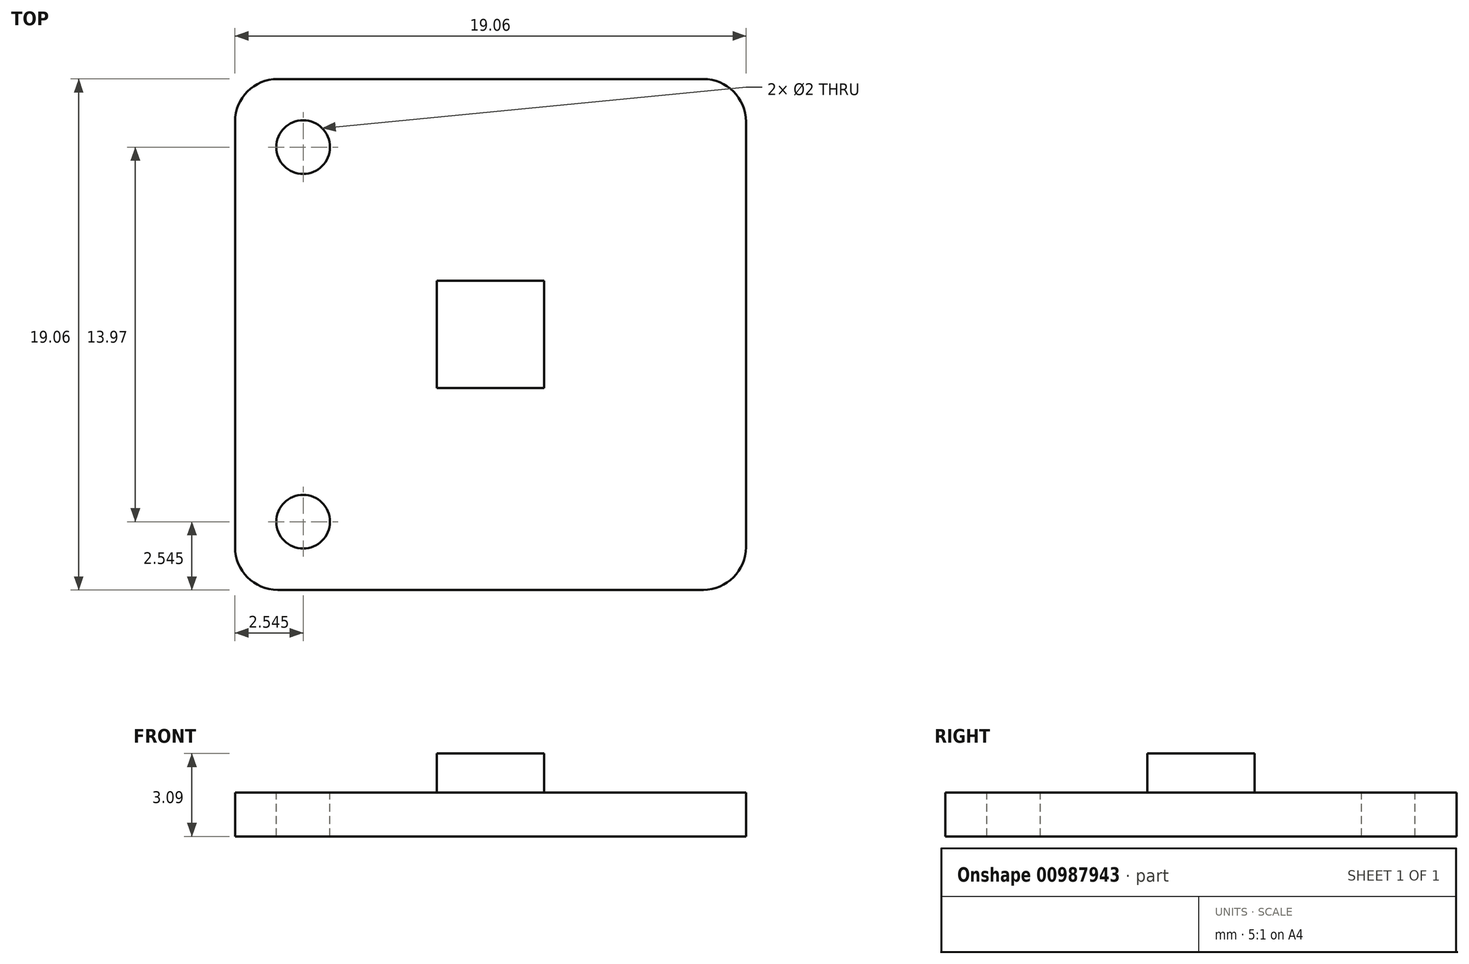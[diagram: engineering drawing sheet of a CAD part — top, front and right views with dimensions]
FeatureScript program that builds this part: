
annotation { "Feature Type Name" : "Feature", "Feature Type Description" : "" }
export const myFeature = defineFeature(function(context is Context, id is Id, definition is map)
    precondition{}
    {
        {
            var Q0;
            Q0=qCreatedBy(makeId("Top.planeOp"),FACE);
            var sketch = newSketch(context, id + "F0", { "sketchPlane" : qUnion([Q0])});
            skLineSegment(sketch, "E0.bottom", {"start": v(9.53, 9.52) * mm, "end": v(-9.53, 9.52) * mm});
            skLineSegment(sketch, "E0.top", {"start": v(9.53, -9.53) * mm, "end": v(-9.53, -9.53) * mm});
            skLineSegment(sketch, "E0.left", {"start": v(9.53, 9.52) * mm, "end": v(9.53, -9.53) * mm});
            skLineSegment(sketch, "E0.right", {"start": v(-9.53, 9.53) * mm, "end": v(-9.53, -9.53) * mm});
            skPoint(sketch, "E0.middle", {"position": v(0, 0) * mm});
            skSolve(sketch);
        }
        {
            var Q0;
            Q0 = qSketchRegion(id + "F0", true);
            extrude(context, id + "F1", {"entities" : qUnion([Q0]), "depth" : 1.64 * mm, "offsetDistance" : 25.4 * mm});
        }
        {
            var Q0;
            Q0=makeQuery(id+"F1.opExtrude","SWEPT_EDGE",EDGE,{"disambiguationData":[OSD([sQuery(id+"F0.wireOp",EDGE,"E0.bottom"),sQuery(id+"F0.wireOp",EDGE,"E0.right")])]});
            var Q1;
            Q1=makeQuery(id+"F1.opExtrude","SWEPT_EDGE",EDGE,{"disambiguationData":[OSD([sQuery(id+"F0.wireOp",EDGE,"E0.bottom"),sQuery(id+"F0.wireOp",EDGE,"E0.left")])]});
            var Q2;
            Q2=makeQuery(id+"F1.opExtrude","SWEPT_EDGE",EDGE,{"disambiguationData":[OSD([sQuery(id+"F0.wireOp",EDGE,"E0.top"),sQuery(id+"F0.wireOp",EDGE,"E0.left")])]});
            var Q3;
            Q3=makeQuery(id+"F1.opExtrude","SWEPT_EDGE",EDGE,{"disambiguationData":[OSD([sQuery(id+"F0.wireOp",EDGE,"E0.top"),sQuery(id+"F0.wireOp",EDGE,"E0.right")])]});
            fillet(context, id + "F2", {"entities" : qUnion([Q0, Q1, Q2, Q3]), "radius" : 1.59 * mm, "tangentPropagation" : true, "allowEdgeOverflow" : false});
        }
        {
            var Q0;
            Q0=makeQuery(id+"F1.opExtrude","CAP_FACE",FACE,{"disambiguationData":[OSD([sQuery(id+"F0.wireOp",EDGE,"E0.bottom"),sQuery(id+"F0.wireOp",EDGE,"E0.top"),sQuery(id+"F0.wireOp",EDGE,"E0.left"),sQuery(id+"F0.wireOp",EDGE,"E0.right")])],"isStart":false});
            var sketch = newSketch(context, id + "F3", { "sketchPlane" : qUnion([Q0])});
            skCircle(sketch, "E1", {"center": v(-6.99, 6.99) * mm, "radius": 1 * mm});
            skCircle(sketch, "E2.MirrorC", {"center": v(-6.99, -6.99) * mm, "radius": 1 * mm});
            skSolve(sketch);
        }
        {
            var Q0;
            Q0 = qSketchRegion(id + "F3", true);
            extrude(context, id + "F4", {"entities" : qUnion([Q0]), "operationType" : NewBodyOperationType.REMOVE, "endBound" : BoundingType.THROUGH_ALL, "oppositeDirection" : true, "depth" : 25.4 * mm, "offsetDistance" : 25.4 * mm});
        }
        {
            var Q0;
            Q0=makeQuery(id+"F1.opExtrude","CAP_FACE",FACE,{"disambiguationData":[OSD([sQuery(id+"F0.wireOp",EDGE,"E0.bottom"),sQuery(id+"F0.wireOp",EDGE,"E0.top"),sQuery(id+"F0.wireOp",EDGE,"E0.left"),sQuery(id+"F0.wireOp",EDGE,"E0.right")])],"isStart":false});
            var sketch = newSketch(context, id + "F5", { "sketchPlane" : qUnion([Q0])});
            skLineSegment(sketch, "E3.bottom", {"start": v(2, 2) * mm, "end": v(-2, 2) * mm});
            skLineSegment(sketch, "E3.top", {"start": v(2, -2) * mm, "end": v(-2, -2) * mm});
            skLineSegment(sketch, "E3.left", {"start": v(2, 2) * mm, "end": v(2, -2) * mm});
            skLineSegment(sketch, "E3.right", {"start": v(-2, 2) * mm, "end": v(-2, -2) * mm});
            skPoint(sketch, "E3.middle", {"position": v(0, 0) * mm});
            skSolve(sketch);
        }
        {
            var Q0;
            Q0 = qSketchRegion(id + "F5", true);
            extrude(context, id + "F6", {"entities" : qUnion([Q0]), "operationType" : NewBodyOperationType.ADD, "depth" : 1.45 * mm, "offsetDistance" : 25.4 * mm});
        }
    });
